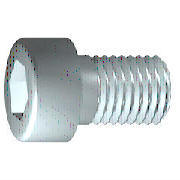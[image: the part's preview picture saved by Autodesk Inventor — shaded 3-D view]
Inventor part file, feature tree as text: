
AUTODESK INVENTOR PART (.ipt)
format: ipt  version: 2022.1 (Build 261234000, 234)  size: 186,880 bytes
history: native  units: mm (DEFAULTED — no unit token found)
features: sketch x2, other x1, extrude x1, plane x1, fillet x1
ambient origin geometry x7: Origin, YZ Plane, XY Plane, X Axis, Y Axis, Z Axis, Center Point
bodies: Solid1 (feature_tree)
feature tree (6):
  other  "Cuerpo"
  extrude  "Ranura"  Depth=4.0mm
  plane  "Work Plane1"
  fillet  "Fillet2"  Radius=4.0mm
  sketch  "Boceto1"  dims[d1=20.0mm d2=0.429515mm d3=4.0mm]
  sketch  "Boceto2"  dims[d4=2.0mm d5=60.0deg d6=4.0mm d7=4.0mm d8=3.464102mm d9=7.0mm d10=90.0deg d11=10.0mm d12=0.0mm d13=20.0mm d14=0.0mm d15=0.429415mm d16=0.429415mm d17=0.4mm d19=0.0mm d26=35.0mm d27=45.0deg d28=0.0mm d29=0.0mm d30=0.1mm]
